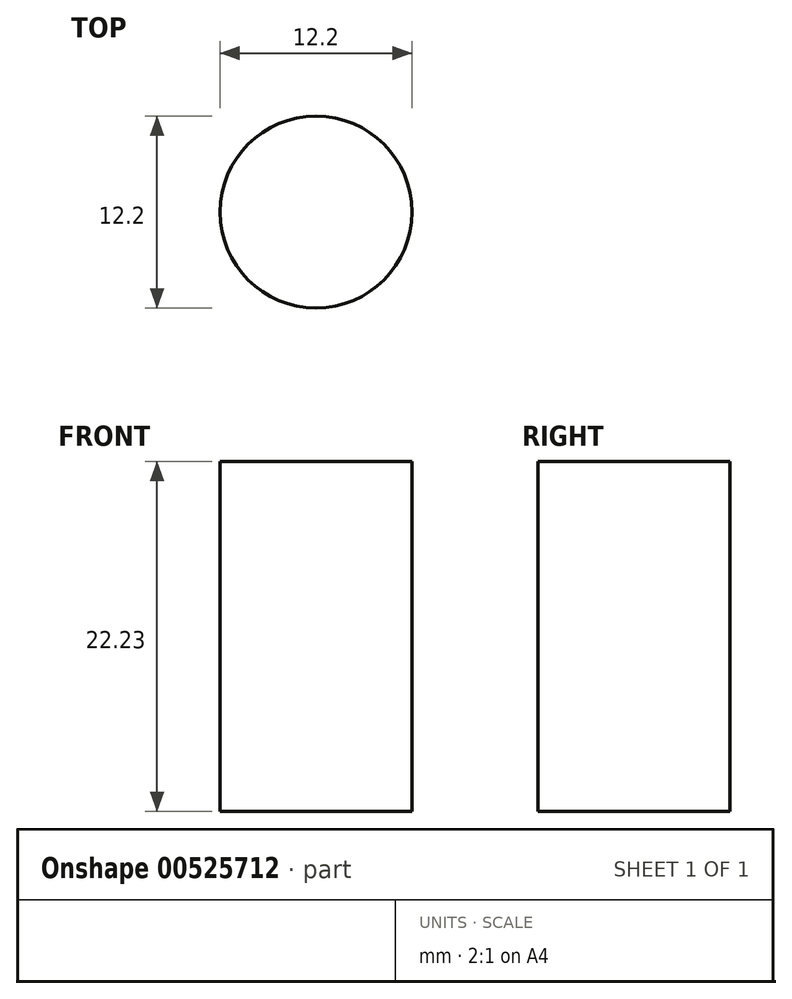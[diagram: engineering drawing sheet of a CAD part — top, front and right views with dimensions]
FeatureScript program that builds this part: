
annotation { "Feature Type Name" : "Feature", "Feature Type Description" : "" }
export const myFeature = defineFeature(function(context is Context, id is Id, definition is map)
    precondition{}
    {
        {
            var Q0;
            Q0=qCreatedBy(makeId("Top.planeOp"),FACE);
            var sketch = newSketch(context, id + "F0", { "sketchPlane" : qUnion([Q0])});
            skCircle(sketch, "E0", {"center": v(0, 0) * mm, "radius": 6.1 * mm});
            skSolve(sketch);
        }
        {
            var Q0;
            Q0 = qSketchRegion(id + "F0", true);
            extrude(context, id + "F1", {"entities" : qUnion([Q0]), "depth" : 22.22 * mm, "offsetDistance" : 25.4 * mm});
        }
    });
